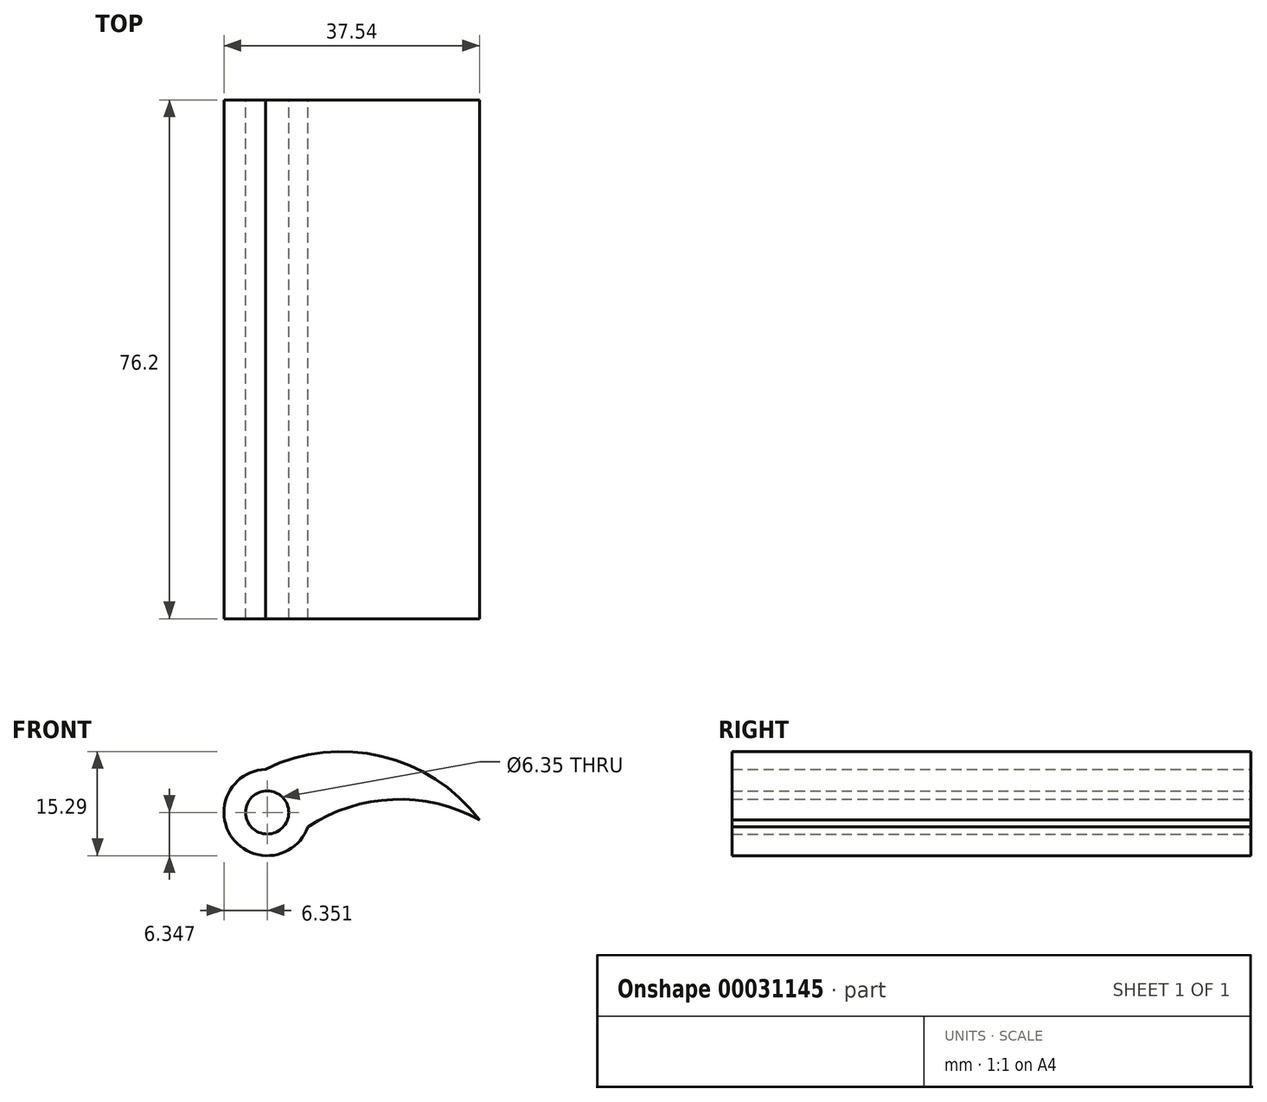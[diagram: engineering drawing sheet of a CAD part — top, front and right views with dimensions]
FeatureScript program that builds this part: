
annotation { "Feature Type Name" : "Feature", "Feature Type Description" : "" }
export const myFeature = defineFeature(function(context is Context, id is Id, definition is map)
    precondition{}
    {
        {
            var Q0;
            Q0=qCreatedBy(makeId("Front.planeOp"),FACE);
            var sketch = newSketch(context, id + "F0", { "sketchPlane" : qUnion([Q0])});
            skArc(sketch, "E0", {"start": v(-74.11, 36.31) * mm, "mid": v(-69.05, 43.28) * mm, "end": v(-75.6, 48.88) * mm});
            skArc(sketch, "E1", {"start": v(-44.17, 41.42) * mm, "mid": v(-58.55, 50.8) * mm, "end": v(-75.6, 48.88) * mm});
            skArc(sketch, "E2", {"start": v(-44.17, 41.42) * mm, "mid": v(-60.04, 44.12) * mm, "end": v(-74.11, 36.31) * mm});
            skCircle(sketch, "E3", {"center": v(-75.36, 42.54) * mm, "radius": 6.35 * mm});
            skCircle(sketch, "E4", {"center": v(-75.36, 42.54) * mm, "radius": 3.18 * mm});
            skSolve(sketch);
        }
        {
            var Q0;
            Q0 = qSketchRegion(id + "F0", true);
            extrude(context, id + "F1", {"entities" : qUnion([Q0]), "depth" : 76.2 * mm});
        }
    });
